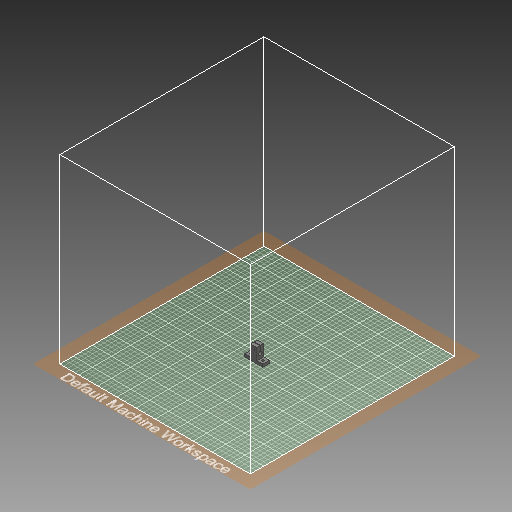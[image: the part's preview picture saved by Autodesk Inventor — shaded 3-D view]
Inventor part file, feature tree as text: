
AUTODESK INVENTOR PART (.ipt)
format: ipt  version: 2019 (Build 230136000, 136)  size: 317,440 bytes
history: native  units: in
note: dims shown in document units (in); Inventor stores cm internally (conversion verified against a paired STEP export)
features: extrude x5, sketch x5
ambient origin geometry x8: Origin, YZ Plane, XZ Plane, XY Plane, X Axis, Y Axis, Z Axis, Center Point
bodies: Solid1 (feature_tree)
feature tree (10):
  extrude  "Extrusion1"  Depth=0.5906in
  extrude  "Extrusion2"  Depth=0.5512in
  extrude  "Extrusion4"  Depth=0.9843in
  extrude  "Extrusion5"  Depth=1.1811in TaperAngle=0.0deg
  extrude  "Extrusion6"  Depth=0.2362in
  sketch  "Sketch1"  dims[d0=1.5748in d1=0.5906in]
  sketch  "Sketch2"  dims[d2=0.2362in d3=0.0in d4=0.5512in]
  sketch  "Sketch4"  dims[d5=0.9843in d6=0.0in d12=0.1673in]
  sketch  "Sketch5"  dims[d13=0.1673in d14=1.1811in d15=0.0in]
  sketch  "Sketch6"  dims[d16=0.315in d17=0.6299in d18=0.0394in d19=1.1811in d20=0.0in d21=0.1673in d22=0.2362in d23=1.1811in d24=0.0in]
